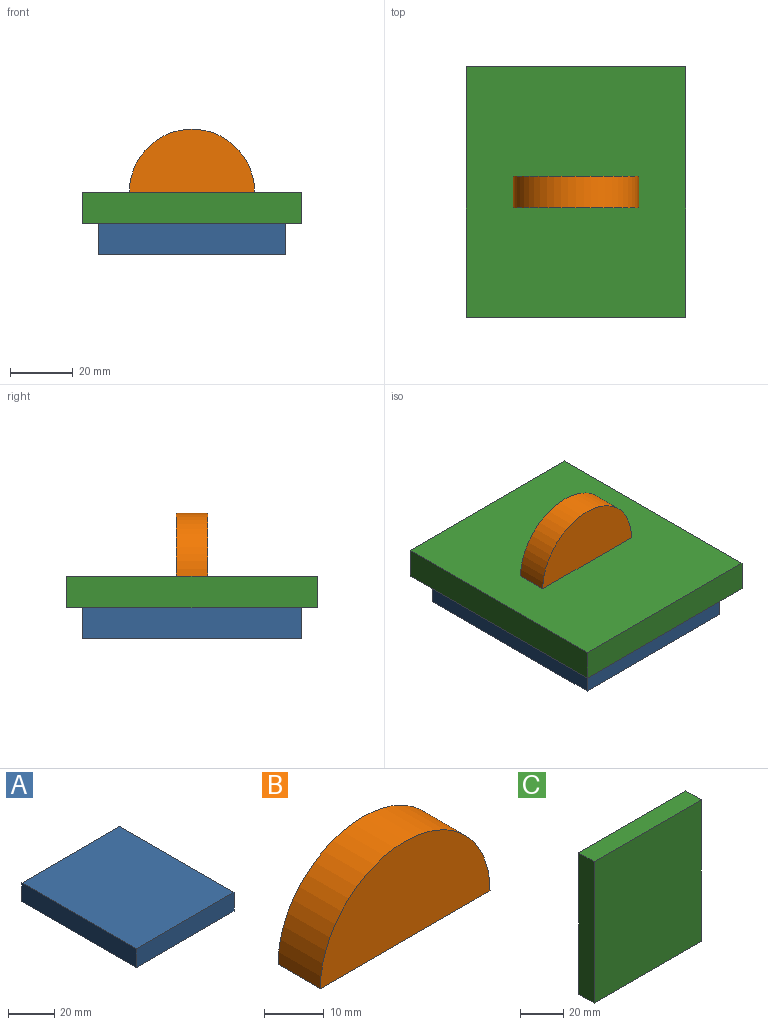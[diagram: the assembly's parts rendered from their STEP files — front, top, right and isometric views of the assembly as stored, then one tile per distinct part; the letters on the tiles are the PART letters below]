
ASSEMBLY  parts=3 mates=2
PART A: 6 faces, bbox 60x70x10 mm
  f0: plane 70x10mm, normal (1,0,0), area 700mm2, adj f1,f3,f4,f5
  f1: plane 70x60mm, normal (0,0,1), area 4200mm2, adj f0,f2,f4,f5
  f2: plane 70x10mm, normal (-1,0,0), area 700mm2, adj f1,f3,f4,f5
  f3: plane 70x60mm, normal (0,0,-1), area 4200mm2, adj f0,f2,f4,f5
  f4: plane 60x10mm, normal (0,-1,0), area 600mm2, adj f0,f1,f2,f3
  f5: plane 60x10mm, normal (0,1,0), area 600mm2, adj f0,f1,f2,f3
PART B: 4 faces, bbox 40x10x20.1 mm
  f0: plane 40x10mm, normal (0,0,-1), area 400mm2, adj f1,f2,f3
  f1: cylinder r=20mm len=40mm, axis (0,1,0), area 630.9mm2, adj f0,f2,f3
  f2: plane 40x20.13mm, normal (0,-1,0), area 633.6mm2, adj f0,f1
  f3: plane 40x20.13mm, normal (0,1,0), area 633.6mm2, adj f0,f1
PART C: 6 faces, bbox 70x10x80 mm
  f0: plane 80x70mm, normal (0,1,0), area 5600mm2, adj f1,f3,f4,f5
  f1: plane 80x10mm, normal (-1,0,0), area 800mm2, adj f0,f2,f4,f5
  f2: plane 80x70mm, normal (0,-1,0), area 5600mm2, adj f1,f3,f4,f5
  f3: plane 80x10mm, normal (1,0,0), area 800mm2, adj f0,f2,f4,f5
  f4: plane 70x10mm, normal (0,0,1), area 700mm2, adj f0,f1,f2,f3
  f5: plane 70x10mm, normal (0,0,-1), area 700mm2, adj f0,f1,f2,f3
PLACE A rot(axis=(1,0,0),180deg) t=(-49.88,-72.09,23.08)mm
PLACE B t=(-50.08,-32.09,38.08)mm
PLACE C rot(axis=(1,0,0),90deg) t=(-49.88,2.91,33.08)mm
MATE fastened C.f2 <-> A.f3  axis (0,0,-1) through (-49.88,-37.09,28.08)mm
MATE fastened C.f0 <-> B.f0  axis (0,0,1) through (-49.88,-37.09,38.08)mm
